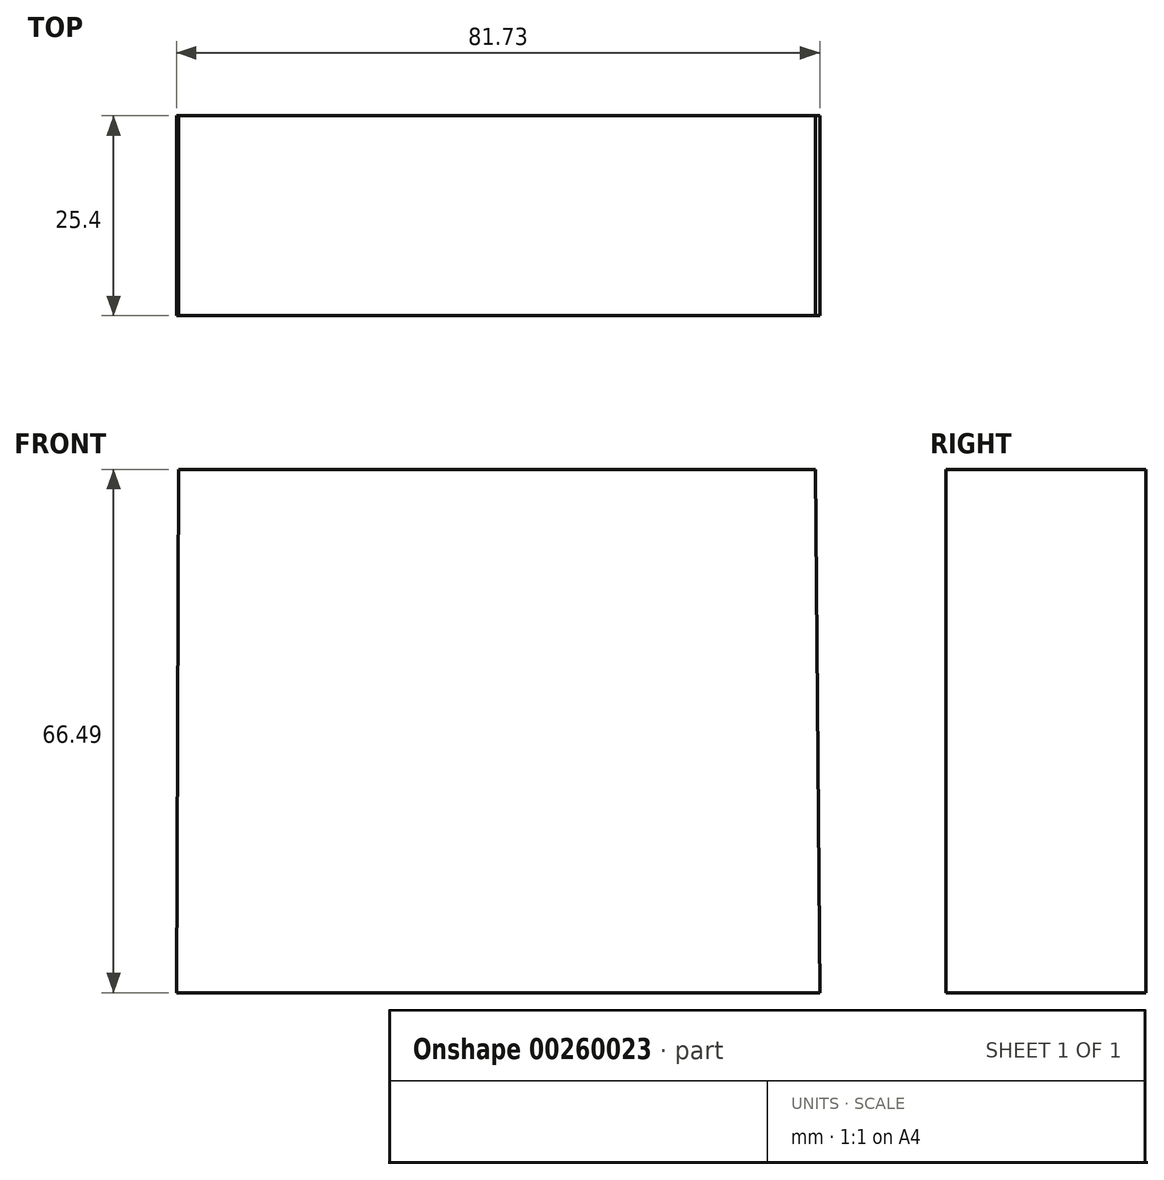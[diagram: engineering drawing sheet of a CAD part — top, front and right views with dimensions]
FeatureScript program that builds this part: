
annotation { "Feature Type Name" : "Feature", "Feature Type Description" : "" }
export const myFeature = defineFeature(function(context is Context, id is Id, definition is map)
    precondition{}
    {
        {
            var Q0;
            Q0=qCreatedBy(makeId("Front.planeOp"),FACE);
            var sketch = newSketch(context, id + "F0", { "sketchPlane" : qUnion([Q0])});
            skLineSegment(sketch, "E0", {"start": v(-40.29, 47.61) * mm, "end": v(-40.57, -19.72) * mm});
            skLineSegment(sketch, "E1", {"start": v(-40.29, 47.61) * mm, "end": v(40.62, 47.61) * mm});
            skLineSegment(sketch, "E2", {"start": v(40.62, 47.61) * mm, "end": v(41.18, -20.28) * mm});
            skLineSegment(sketch, "E3", {"start": v(41.18, -18.88) * mm, "end": v(-40.57, -18.88) * mm});
            skSolve(sketch);
        }
        {
            var Q0;
            Q0 = qSketchRegion(id + "F0", true);
            extrude(context, id + "F1", {"entities" : qUnion([Q0]), "depth" : 25.4 * mm});
        }
    });
